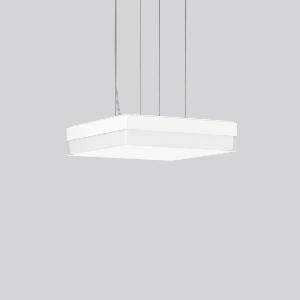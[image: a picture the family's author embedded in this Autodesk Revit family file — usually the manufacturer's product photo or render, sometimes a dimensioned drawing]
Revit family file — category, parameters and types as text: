
# Revit family: flat_slim_square_312542_002_730_6682
name_source: partatom
category: Lighting Fixtures
units: mm (PartAtom-declared; Revit-internal decimal feet)

## family parameters
Cut with Voids When Loaded = No
Host = Face
Light Source = No
Part Type = Normal
Room Calculation Point = No
Round Connector Dimension = Use Diameter
Shared = No

## types (1)
- MultiLumen 2 840 (1 x LED Modul 840, 2300 lm, 4000)
    Apparent Load = 21 VA
    CIE Flux Codes = 43 75 93 91 100
    Color Rendering = 80
    Color Temperature = 4000
    Default Elevation = 1800 mm
    Height = 70 mm
    Lamp = 1 x LED Modul 840
    Lamp Light Flux = 2300 lm
    Lamp count = 1
    Length = 300 mm
    Lifetime = 50000 h
    Luminous efficacy = 110 lm/W
    Manufacturer = RZB
    ModVariant = No
    Model = 312542.002.730
    Mounting Place = Ceiling
    Mounting Type = Pendant
    Number of Poles = 1
    OnlyDefault = Yes
    Power Factor = 1
    Product Name = FLAT SLIM square
    Product group = Pendant luminaires
    ProductGroupID = 902
    Protection Class = Protection class I
    Protection Degree = IP 40
    RLX_Detail_Level = 1
    RLX_Emergency_Light_Flux = 0 lm
    RLX_Emergency_Type = 0
    RLX_Emergency_Type_DB = No
    RlxData = <blob elided: 13861 chars, md5=2d37fb68>
    Socket = socket
    Standby Power = 0 W
    System Light Flux = 2300 lm
    System Power = 21 W
    Type Comments = MultiLumen 2 840
    Type Image = 312542.002.jpg
    URL = http://relux.com
    VarID = multilumen_2_840
    Voltage = 230 V
    Voltage Range = 220-240 V
    Weight = 0.00 kg
    Width = 300 mm

## geometry (parser evidence)
native form markers: Sweep x14
no freeform markers — native parametric forms only
